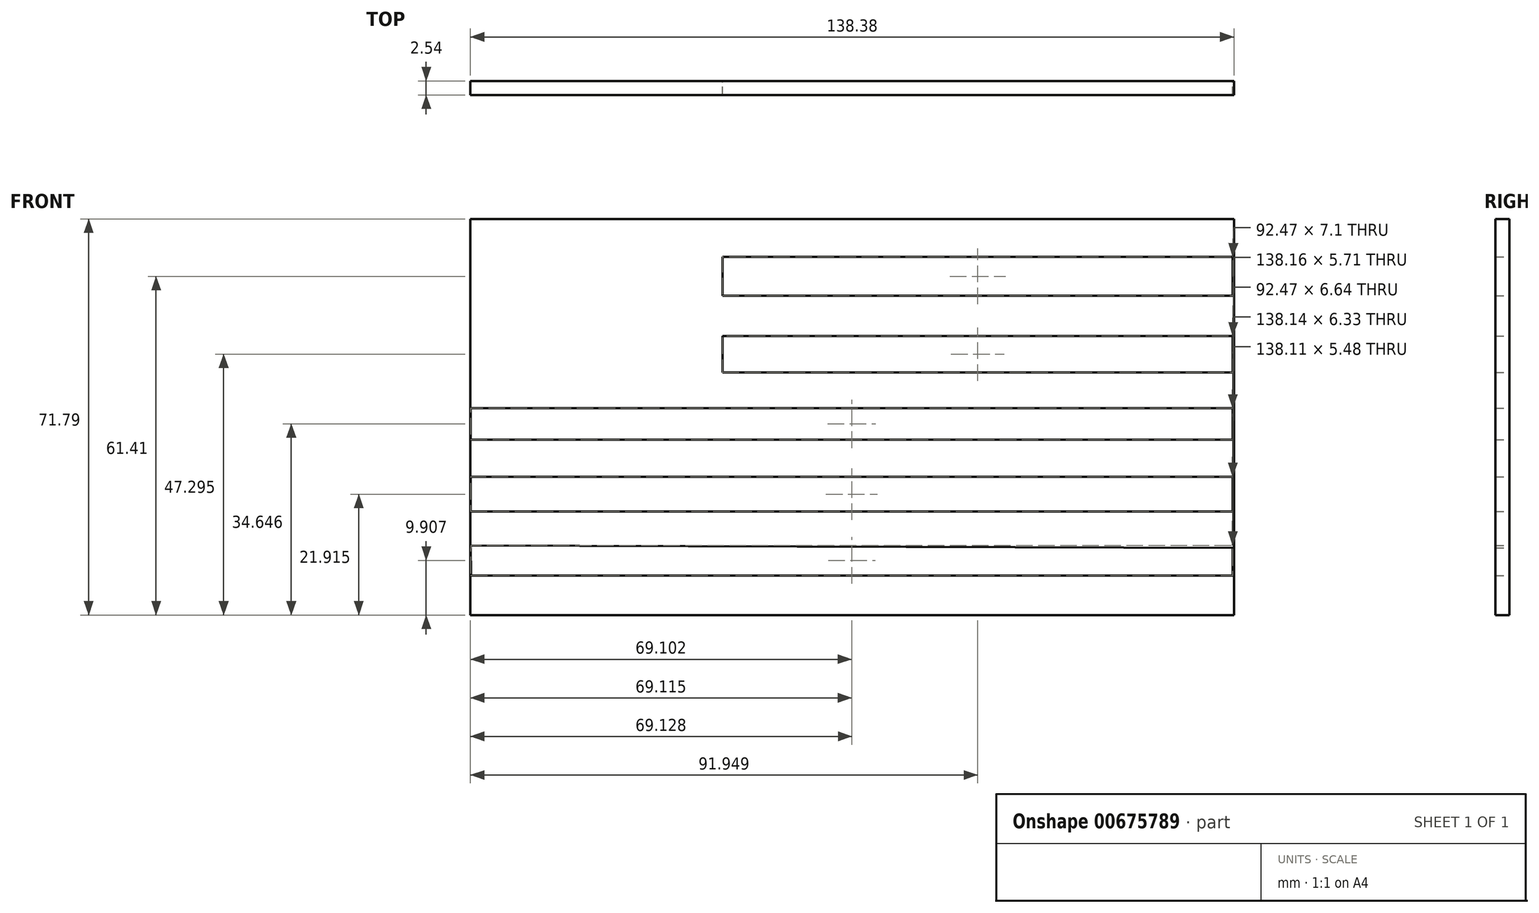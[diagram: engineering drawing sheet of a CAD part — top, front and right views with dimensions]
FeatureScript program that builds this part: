
annotation { "Feature Type Name" : "Feature", "Feature Type Description" : "" }
export const myFeature = defineFeature(function(context is Context, id is Id, definition is map)
    precondition{}
    {
        {
            var Q0;
            Q0=qCreatedBy(makeId("Front.planeOp"),FACE);
            var sketch = newSketch(context, id + "F0", { "sketchPlane" : qUnion([Q0])});
            skLineSegment(sketch, "E0.bottom", {"start": v(-69.2, -37.5) * mm, "end": v(69.2, -37.5) * mm});
            skLineSegment(sketch, "E0.top", {"start": v(-69.2, 34.29) * mm, "end": v(69.2, 34.29) * mm});
            skLineSegment(sketch, "E0.left", {"start": v(-69.2, -37.5) * mm, "end": v(-69.2, 34.29) * mm});
            skLineSegment(sketch, "E0.right", {"start": v(69.2, -37.5) * mm, "end": v(69.2, 34.29) * mm});
            skPoint(sketch, "E0.middle", {"position": v(0, -1.6) * mm});
            skLineSegment(sketch, "E1", {"start": v(-69.2, 0) * mm, "end": v(-23.48, 0) * mm});
            skLineSegment(sketch, "E2", {"start": v(-23.48, 0) * mm, "end": v(-23.48, 34.29) * mm});
            skLineSegment(sketch, "E3", {"start": v(-23.48, 0) * mm, "end": v(69.79, 0) * mm});
            skLineSegment(sketch, "E4", {"start": v(-23.48, 27.46) * mm, "end": v(69.2, 27.46) * mm});
            skLineSegment(sketch, "E5", {"start": v(-23.48, 20.36) * mm, "end": v(69.2, 20.36) * mm});
            skLineSegment(sketch, "E6", {"start": v(-23.48, 13.12) * mm, "end": v(69.2, 13.12) * mm});
            skLineSegment(sketch, "E7", {"start": v(-23.48, 6.47) * mm, "end": v(69.2, 6.47) * mm});
            skLineSegment(sketch, "E8", {"start": v(-69.16, -5.7) * mm, "end": v(69.2, -5.7) * mm});
            skLineSegment(sketch, "E9", {"start": v(-69.14, -12.44) * mm, "end": v(69.2, -12.42) * mm});
            skLineSegment(sketch, "E10", {"start": v(-69.13, -18.75) * mm, "end": v(69.2, -18.75) * mm});
            skLineSegment(sketch, "E11", {"start": v(-69.12, -24.85) * mm, "end": v(69.2, -25.31) * mm});
            skLineSegment(sketch, "E12", {"start": v(-69.1, -30.33) * mm, "end": v(69.2, -30.33) * mm});
            skLineSegment(sketch, "E13", {"start": v(-69.17, 0) * mm, "end": v(-69.1, -37.5) * mm});
            skLineSegment(sketch, "E14", {"start": v(69, -37.5) * mm, "end": v(69, 34.29) * mm});
            skSolve(sketch);
        }
        {
            var Q0;
            {var subQ0=sQuery(id+"F0.wireOp",EDGE,"E0.right");var subQ1=sQuery(id+"F0.wireOp",EDGE,"E0.top");var subQ2=makeQuery(id+"F0.imprint","INTERSECT",VERTEX,{"derivedFrom":[subQ1,subQ0]});Q0=makeQuery(id+"F0.imprint","IMPRINT",FACE,{"disambiguationData":[TD([[makeQuery(id+"F0.imprint","IMPRINT",EDGE,{"disambiguationData":[TD([[subQ2,1.0]])],"derivedFrom":subQ1}),-1.0]])]});}
            var Q1;
            {var subQ0=sQuery(id+"F0.wireOp",EDGE,"E2");var subQ1=sQuery(id+"F0.wireOp",EDGE,"E0.top");var subQ2=makeQuery(id+"F0.imprint","INTERSECT",VERTEX,{"derivedFrom":[subQ1,subQ0]});Q1=makeQuery(id+"F0.imprint","IMPRINT",FACE,{"disambiguationData":[TD([[makeQuery(id+"F0.imprint","IMPRINT",EDGE,{"disambiguationData":[TD([[subQ2,-1.0]])],"derivedFrom":subQ1}),-1.0]])]});}
            var Q2;
            {var subQ0=sQuery(id+"F0.wireOp",EDGE,"E7");var subQ1=sQuery(id+"F0.wireOp",EDGE,"E0.right");var subQ2=makeQuery(id+"F0.imprint","INTERSECT",VERTEX,{"derivedFrom":[subQ1,subQ0]});Q2=makeQuery(id+"F0.imprint","IMPRINT",FACE,{"disambiguationData":[TD([[makeQuery(id+"F0.imprint","IMPRINT",EDGE,{"disambiguationData":[TD([[subQ2,1.0]])],"derivedFrom":subQ1}),1.0]])]});}
            var Q3;
            {var subQ1=sQuery(id+"F0.wireOp",EDGE,"E2");var subQ3=sQuery(id+"F0.wireOp",EDGE,"E7");var subQ4=makeQuery(id+"F0.imprint","INTERSECT",VERTEX,{"derivedFrom":[subQ1,subQ3]});Q3=makeQuery(id+"F0.imprint","IMPRINT",FACE,{"disambiguationData":[TD([[makeQuery(id+"F0.imprint","IMPRINT",EDGE,{"disambiguationData":[TD([[subQ4,-1.0]])],"derivedFrom":subQ3}),-1.0]])]});}
            var Q4;
            {var subQ4=sQuery(id+"F0.wireOp",EDGE,"E0.left");var subQ6=sQuery(id+"F0.wireOp",EDGE,"E0.top");var subQ7=makeQuery(id+"F0.imprint","INTERSECT",VERTEX,{"derivedFrom":[subQ6,subQ4]});Q4=makeQuery(id+"F0.imprint","IMPRINT",FACE,{"disambiguationData":[TD([[makeQuery(id+"F0.imprint","IMPRINT",EDGE,{"disambiguationData":[TD([[subQ7,-1.0]])],"derivedFrom":subQ6}),-1.0]])]});}
            var Q5;
            {var subQ0=sQuery(id+"F0.wireOp",EDGE,"E8");var subQ1=sQuery(id+"F0.wireOp",EDGE,"E0.right");var subQ2=makeQuery(id+"F0.imprint","INTERSECT",VERTEX,{"derivedFrom":[subQ1,subQ0]});Q5=makeQuery(id+"F0.imprint","IMPRINT",FACE,{"disambiguationData":[TD([[makeQuery(id+"F0.imprint","IMPRINT",EDGE,{"disambiguationData":[TD([[subQ2,1.0]])],"derivedFrom":subQ1}),1.0]])]});}
            var Q6;
            {var subQ0=sQuery(id+"F0.wireOp",EDGE,"SBRN85CN-4Pm9-gWoy-6hLh-DhKFFLTnaMFS");var subQ1=sQuery(id+"F0.wireOp",EDGE,"E8");var subQ2=makeQuery(id+"F0.imprint","INTERSECT",VERTEX,{"derivedFrom":[subQ1,subQ0]});Q6=makeQuery(id+"F0.imprint","IMPRINT",FACE,{"disambiguationData":[TD([[makeQuery(id+"F0.imprint","IMPRINT",EDGE,{"disambiguationData":[TD([[subQ2,-1.0]])],"derivedFrom":subQ1}),-1.0]])]});}
            var Q7;
            {var subQ0=sQuery(id+"F0.wireOp",EDGE,"E10");var subQ1=sQuery(id+"F0.wireOp",EDGE,"E0.right");var subQ2=makeQuery(id+"F0.imprint","INTERSECT",VERTEX,{"derivedFrom":[subQ1,subQ0]});Q7=makeQuery(id+"F0.imprint","IMPRINT",FACE,{"disambiguationData":[TD([[makeQuery(id+"F0.imprint","IMPRINT",EDGE,{"disambiguationData":[TD([[subQ2,1.0]])],"derivedFrom":subQ1}),1.0]])]});}
            var Q8;
            {var subQ0=sQuery(id+"F0.wireOp",EDGE,"SBRN85CN-4Pm9-gWoy-6hLh-DhKFFLTnaMFS");var subQ1=sQuery(id+"F0.wireOp",EDGE,"E10");var subQ2=makeQuery(id+"F0.imprint","INTERSECT",VERTEX,{"derivedFrom":[subQ1,subQ0]});Q8=makeQuery(id+"F0.imprint","IMPRINT",FACE,{"disambiguationData":[TD([[makeQuery(id+"F0.imprint","IMPRINT",EDGE,{"disambiguationData":[TD([[subQ2,-1.0]])],"derivedFrom":subQ1}),-1.0]])]});}
            var Q9;
            {var subQ0=sQuery(id+"F0.wireOp",EDGE,"E0.right");var subQ1=sQuery(id+"F0.wireOp",EDGE,"E0.bottom");var subQ2=makeQuery(id+"F0.imprint","INTERSECT",VERTEX,{"derivedFrom":[subQ1,subQ0]});Q9=makeQuery(id+"F0.imprint","IMPRINT",FACE,{"disambiguationData":[TD([[makeQuery(id+"F0.imprint","IMPRINT",EDGE,{"disambiguationData":[TD([[subQ2,1.0]])],"derivedFrom":subQ1}),1.0]])]});}
            var Q10;
            {var subQ0=sQuery(id+"F0.wireOp",EDGE,"SBRN85CN-4Pm9-gWoy-6hLh-DhKFFLTnaMFS");var subQ1=sQuery(id+"F0.wireOp",EDGE,"E0.bottom");var subQ2=makeQuery(id+"F0.imprint","INTERSECT",VERTEX,{"derivedFrom":[subQ1,subQ0]});Q10=makeQuery(id+"F0.imprint","IMPRINT",FACE,{"disambiguationData":[TD([[makeQuery(id+"F0.imprint","IMPRINT",EDGE,{"disambiguationData":[TD([[subQ2,-1.0]])],"derivedFrom":subQ1}),1.0]])]});}
            var Q11;
            {var subQ0=sQuery(id+"F0.wireOp",EDGE,"E4");var subQ1=sQuery(id+"F0.wireOp",EDGE,"E0.right");var subQ2=makeQuery(id+"F0.imprint","INTERSECT",VERTEX,{"derivedFrom":[subQ1,subQ0]});Q11=makeQuery(id+"F0.imprint","IMPRINT",FACE,{"disambiguationData":[TD([[makeQuery(id+"F0.imprint","IMPRINT",EDGE,{"disambiguationData":[TD([[subQ2,1.0]])],"derivedFrom":subQ1}),1.0]])]});}
            var Q12;
            {var subQ0=sQuery(id+"F0.wireOp",EDGE,"E5");var subQ1=sQuery(id+"F0.wireOp",EDGE,"E0.right");var subQ2=makeQuery(id+"F0.imprint","INTERSECT",VERTEX,{"derivedFrom":[subQ1,subQ0]});Q12=makeQuery(id+"F0.imprint","IMPRINT",FACE,{"disambiguationData":[TD([[makeQuery(id+"F0.imprint","IMPRINT",EDGE,{"disambiguationData":[TD([[subQ2,1.0]])],"derivedFrom":subQ1}),1.0]])]});}
            var Q13;
            {var subQ0=sQuery(id+"F0.wireOp",EDGE,"E6");var subQ1=sQuery(id+"F0.wireOp",EDGE,"E0.right");var subQ2=makeQuery(id+"F0.imprint","INTERSECT",VERTEX,{"derivedFrom":[subQ1,subQ0]});Q13=makeQuery(id+"F0.imprint","IMPRINT",FACE,{"disambiguationData":[TD([[makeQuery(id+"F0.imprint","IMPRINT",EDGE,{"disambiguationData":[TD([[subQ2,1.0]])],"derivedFrom":subQ1}),1.0]])]});}
            var Q14;
            {var subQ0=sQuery(id+"F0.wireOp",EDGE,"E8");var subQ1=sQuery(id+"F0.wireOp",EDGE,"E0.right");var subQ2=makeQuery(id+"F0.imprint","INTERSECT",VERTEX,{"derivedFrom":[subQ1,subQ0]});Q14=makeQuery(id+"F0.imprint","IMPRINT",FACE,{"disambiguationData":[TD([[makeQuery(id+"F0.imprint","IMPRINT",EDGE,{"disambiguationData":[TD([[subQ2,-1.0]])],"derivedFrom":subQ1}),1.0]])]});}
            var Q15;
            {var subQ0=sQuery(id+"F0.wireOp",EDGE,"E9");var subQ1=sQuery(id+"F0.wireOp",EDGE,"E0.right");var subQ2=makeQuery(id+"F0.imprint","INTERSECT",VERTEX,{"derivedFrom":[subQ1,subQ0]});Q15=makeQuery(id+"F0.imprint","IMPRINT",FACE,{"disambiguationData":[TD([[makeQuery(id+"F0.imprint","IMPRINT",EDGE,{"disambiguationData":[TD([[subQ2,1.0]])],"derivedFrom":subQ1}),1.0]])]});}
            var Q16;
            {var subQ0=sQuery(id+"F0.wireOp",EDGE,"E11");var subQ1=sQuery(id+"F0.wireOp",EDGE,"E0.right");var subQ2=makeQuery(id+"F0.imprint","INTERSECT",VERTEX,{"derivedFrom":[subQ1,subQ0]});Q16=makeQuery(id+"F0.imprint","IMPRINT",FACE,{"disambiguationData":[TD([[makeQuery(id+"F0.imprint","IMPRINT",EDGE,{"disambiguationData":[TD([[subQ2,1.0]])],"derivedFrom":subQ1}),1.0]])]});}
            var Q17;
            {var subQ1=sQuery(id+"F0.wireOp",EDGE,"E0.left");var subQ6=sQuery(id+"F0.wireOp",EDGE,"E0.bottom");var subQ7=makeQuery(id+"F0.imprint","INTERSECT",VERTEX,{"derivedFrom":[subQ6,subQ1]});Q17=makeQuery(id+"F0.imprint","IMPRINT",FACE,{"disambiguationData":[TD([[makeQuery(id+"F0.imprint","IMPRINT",EDGE,{"disambiguationData":[TD([[subQ7,-1.0]])],"derivedFrom":subQ6}),1.0]])]});}
            var Q18;
            {var subQ0=sQuery(id+"F0.wireOp",EDGE,"E5");var subQ1=sQuery(id+"F0.wireOp",EDGE,"E2");var subQ2=makeQuery(id+"F0.imprint","INTERSECT",VERTEX,{"derivedFrom":[subQ1,subQ0]});Q18=makeQuery(id+"F0.imprint","IMPRINT",FACE,{"disambiguationData":[TD([[makeQuery(id+"F0.imprint","IMPRINT",EDGE,{"disambiguationData":[TD([[subQ2,1.0]])],"derivedFrom":subQ1}),-1.0]])]});}
            extrude(context, id + "F1", {"entities" : qUnion([Q0, Q1, Q2, Q3, Q4, Q5, Q6, Q7, Q8, Q9, Q10, Q11, Q12, Q13, Q14, Q15, Q16, Q17, Q18]), "endBound" : BoundingType.SYMMETRIC, "depth" : 2.54 * mm, "offsetDistance" : 25.4 * mm});
        }
    });
